# Revit family: NLRS_57_DUF_UN_instortkanaal-manchet-voor-luchtkanaal_LT_velu
name_source: partatom
category: Duct Fittings
units: mm (PartAtom-declared; Revit-internal decimal feet)

## family parameters
Always vertical = Yes
Cut with Voids When Loaded = No
Part Type = Union
Round Connector Dimension = Use Diameter
Shared = No
Work Plane-Based = No

## types (2) — shared parameters
Assembly Code = 57.00
Description = VELU instortkanaal: Rechthoekig verloop
Manufacturer = Velu Klimaattechnische Groothandel
Model = VIK Manchet
NLRS_C_content_datum_gewijzigd = 18-01-2023
NLRS_C_content_provider = Velu Klimaattechnische Groothandel
NLRS_C_content_versie = 3.20.01
NLRS_C_description = VELU instortkanaal: Rechthoekig verloop
Type Comments = Enkel geschikt voor VELU instort kanaal maten
URL = https://webshop.velu.nl
VELU_Article_Data = Manchet
zero-valued in all types: Default Elevation

## per-type parameters (varying)
| type | VELU_Product_Selector |
| Manchet 100 | 1 |
| Manchet 200 | 2 |

## geometry (parser evidence)
native form markers: Sweep x7
no freeform markers — native parametric forms only
